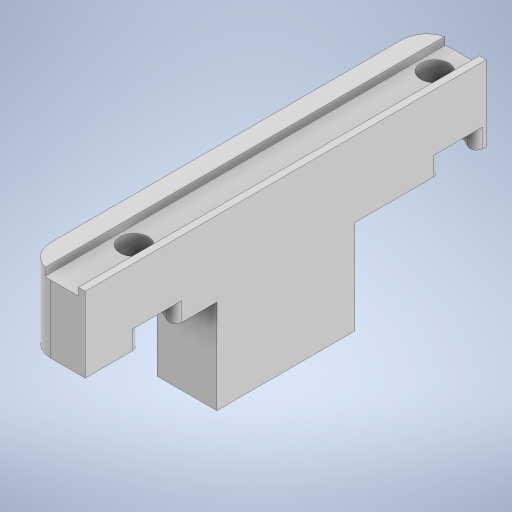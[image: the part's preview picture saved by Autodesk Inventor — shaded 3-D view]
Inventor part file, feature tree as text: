
AUTODESK INVENTOR PART (.ipt)
format: ipt  version: 2024 (Build 280153000, 153)  size: 289,280 bytes
history: native  units: in
note: dims shown in document units (in); Inventor stores cm internally (conversion verified against a paired STEP export)
features: extrude x4, sketch x4, projected_geometry x4, fillet x2
ambient origin geometry x8: Origin, YZ Plane, XZ Plane, XY Plane, X Axis, Y Axis, Z Axis, Center Point
bodies: Solid1 (feature_tree)
feature tree (14):
  extrude  "Extrusion1"  Depth=2.5197in
  extrude  "Extrusion2"  Depth=1.8898in
  extrude  "Extrusion3"  Depth=0.4724in TaperAngle=0.0deg
  fillet  "Fillet1"  Radius=0.0433in
  fillet  "Fillet2"  Radius=0.2126in
  extrude  "Extrusion15"  Depth=0.4724in TaperAngle=0.0deg
  sketch  "Sketch1"  dims[d1=0.374in d2=2.5197in]
  sketch  "Sketch2"  dims[d3=0.1772in d4=1.8898in]
  sketch  "Sketch3"  dims[d6=0.1457in d7=0.4724in d8=0.0in d9=0.0433in d10=0.2126in]
  projected_geometry  "Projected Loop2"
  projected_geometry  "Projected Loop3"
  projected_geometry  "Projected Loop4"
  projected_geometry  "Projected Loop5"
  sketch  "Sketch15"  dims[d11=0.0472in d12=0.4724in d13=0.0in d14=0.2953in d15=0.1181in d16=0.0in d17=0.1772in d18=0.0394in d19=0.1575in d76=0.4724in d79=0.4331in d80=0.8661in d81=0.5906in d82=0.0in d42=0.0197in d43=0.0344in d44=0.0197in d45=0.0344in d46=0.0in d47=0.0in d48=0.0in d49=0.0in d50=0.0in d51=0.0in d52=0.0in d53=0.0in d55=0.0197in d56=0.0344in d57=0.0197in d58=0.0344in d60=0.0197in d61=0.0344in d62=0.0197in d63=0.0344in d72=0.0197in d73=0.0344in d74=0.0197in d75=0.0344in]
